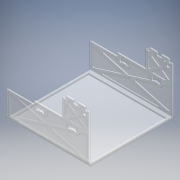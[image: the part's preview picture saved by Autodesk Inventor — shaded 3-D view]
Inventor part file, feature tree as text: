
AUTODESK INVENTOR PART (.ipt)
format: ipt  version: 2016 (Build 200138000, 138)  size: 1,058,304 bytes
history: native  units: mm
features: other x5, sketch x4, extrude x3
ambient origin geometry x8: Origin, YZ Plane, XZ Plane, XY Plane, X Axis, Y Axis, Z Axis, Center Point
bodies: Body1 (feature_tree)
feature tree (12):
  other  "ソリッド1"
  extrude  "押し出し1"  Depth=2.0mm TaperAngle=0.0deg
  extrude  "押し出し2"  Depth=0.5mm TaperAngle=0.0deg
  sketch  "スケッチ3"
  extrude  "押し出し3"  Depth=3.0mm
  other  "曲げパーツ1"
  other  "曲げパーツ2"
  sketch  "スケッチ1"
  sketch  "スケッチ2"
  sketch  "スケッチ4"
  other  "断面エッジを投影1"
  other  "断面エッジを投影2"
